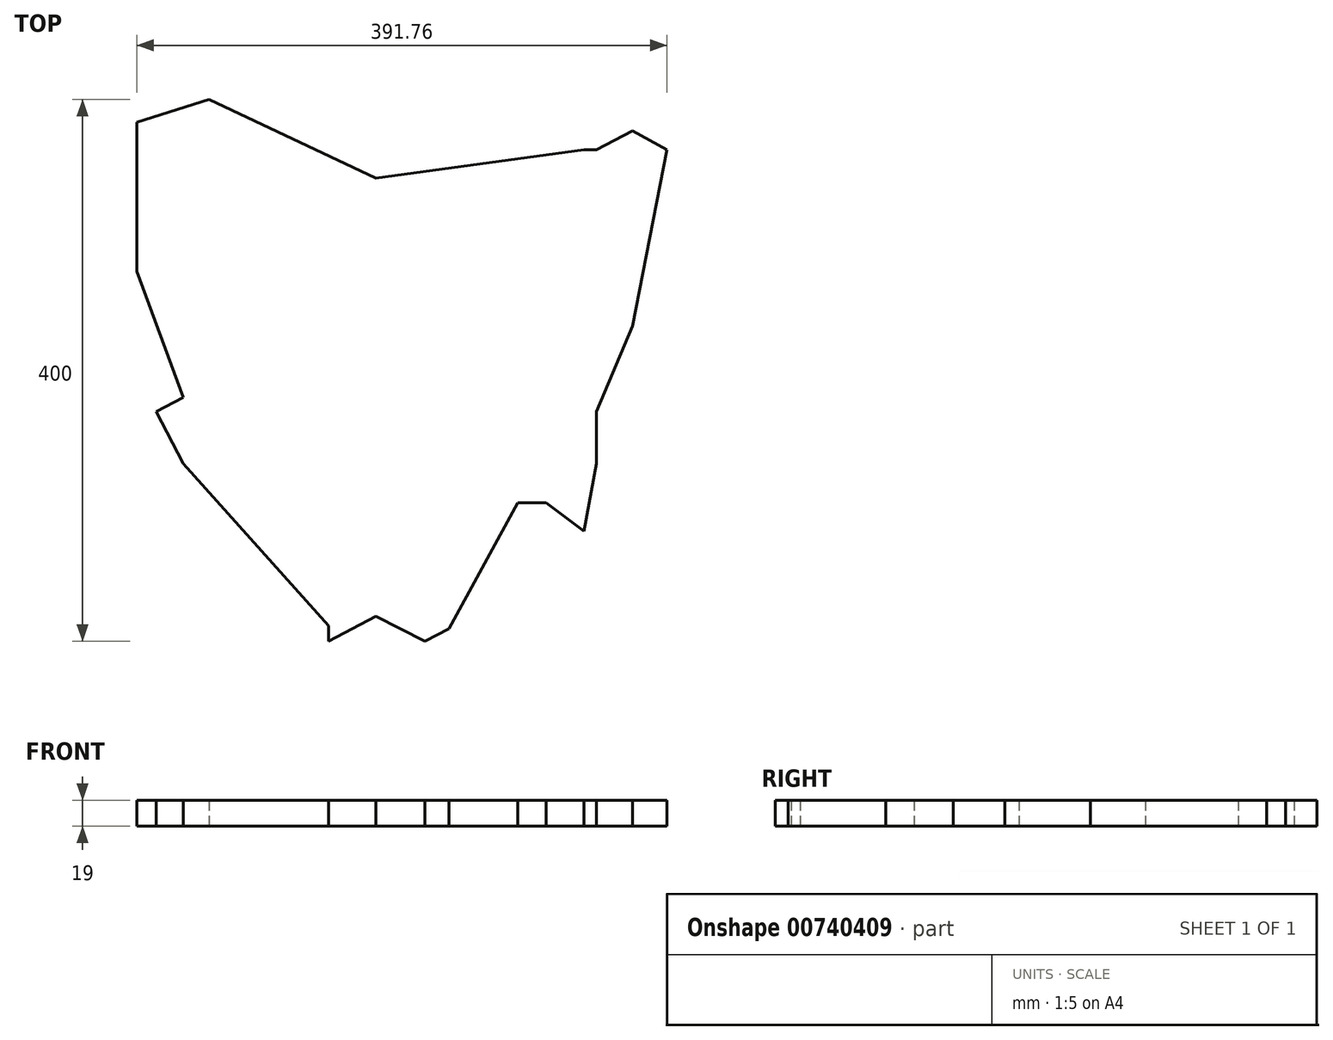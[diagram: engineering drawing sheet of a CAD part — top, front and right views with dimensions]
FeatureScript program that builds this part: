
annotation { "Feature Type Name" : "Feature", "Feature Type Description" : "" }
export const myFeature = defineFeature(function(context is Context, id is Id, definition is map)
    precondition{}
    {
        {
            var Q0;
            Q0=qCreatedBy(makeId("Top.planeOp"),FACE);
            var sketch = newSketch(context, id + "F0", { "sketchPlane" : qUnion([Q0])});
            skLineSegment(sketch, "E0", {"start": v(-177.07, 167.44) * mm, "end": v(-53.82, 109.3) * mm});
            skLineSegment(sketch, "E1", {"start": v(-53.82, 109.3) * mm, "end": v(99.67, 130.23) * mm});
            skLineSegment(sketch, "E2", {"start": v(108.97, 130.23) * mm, "end": v(135.62, 144.26) * mm});
            skLineSegment(sketch, "E3", {"start": v(108.97, 130.23) * mm, "end": v(99.67, 130.23) * mm});
            skLineSegment(sketch, "E4", {"start": v(135.62, 144.26) * mm, "end": v(161.2, 130.23) * mm});
            skLineSegment(sketch, "E5", {"start": v(161.2, 130.23) * mm, "end": v(135.62, 0) * mm});
            skLineSegment(sketch, "E6", {"start": v(135.62, 0) * mm, "end": v(108.97, -63.16) * mm});
            skLineSegment(sketch, "E7", {"start": v(108.97, -63.16) * mm, "end": v(108.97, -101.35) * mm});
            skLineSegment(sketch, "E8", {"start": v(108.97, -101.35) * mm, "end": v(99.67, -151.16) * mm});
            skLineSegment(sketch, "E9", {"start": v(99.67, -151.16) * mm, "end": v(71.76, -130.23) * mm});
            skLineSegment(sketch, "E10", {"start": v(71.76, -130.23) * mm, "end": v(50.83, -130.23) * mm});
            skLineSegment(sketch, "E11", {"start": v(50.83, -130.23) * mm, "end": v(0, -223.26) * mm});
            skLineSegment(sketch, "E12", {"start": v(0, -223.26) * mm, "end": v(-17.67, -232.56) * mm});
            skLineSegment(sketch, "E13", {"start": v(-17.67, -232.56) * mm, "end": v(-53.82, -214.2) * mm});
            skLineSegment(sketch, "E14", {"start": v(-53.82, -214.2) * mm, "end": v(-88.7, -232.56) * mm});
            skLineSegment(sketch, "E15", {"start": v(-88.7, -232.56) * mm, "end": v(-88.7, -221.04) * mm});
            skLineSegment(sketch, "E16", {"start": v(-88.7, -221.04) * mm, "end": v(-196.11, -101.35) * mm});
            skLineSegment(sketch, "E17", {"start": v(-196.11, -101.35) * mm, "end": v(-216.21, -63.16) * mm});
            skLineSegment(sketch, "E18", {"start": v(-216.21, -63.16) * mm, "end": v(-196.11, -52.58) * mm});
            skLineSegment(sketch, "E19", {"start": v(-196.11, -52.58) * mm, "end": v(-230.56, 40.55) * mm});
            skLineSegment(sketch, "E20", {"start": v(-230.56, 40.55) * mm, "end": v(-230.56, 150.63) * mm});
            skLineSegment(sketch, "E21", {"start": v(-230.56, 150.63) * mm, "end": v(-177.07, 167.44) * mm});
            skSolve(sketch);
        }
        {
            var Q0;
            Q0=makeQuery(id+"F0.imprint","IMPRINT",FACE,{"disambiguationData":[TD([[makeQuery(id+"F0.imprint","IMPRINT",EDGE,{"derivedFrom":sQuery(id+"F0.wireOp",EDGE,"E0")}),-1.0]])]});
            extrude(context, id + "F1", {"entities" : qUnion([Q0]), "depth" : 19 * mm, "offsetDistance" : 25 * mm});
        }
    });
